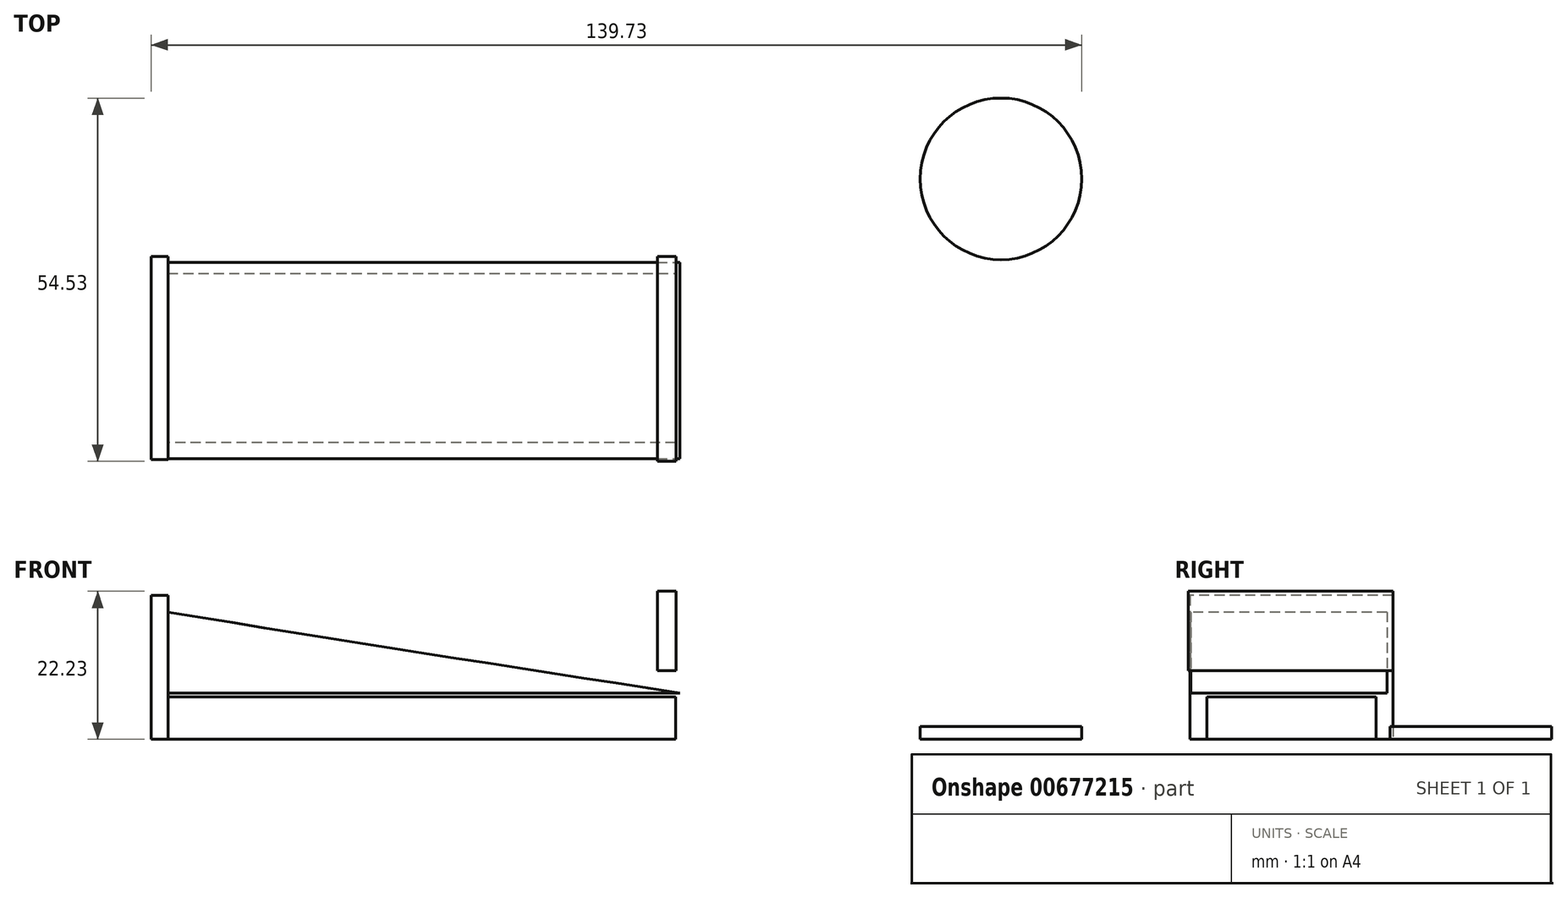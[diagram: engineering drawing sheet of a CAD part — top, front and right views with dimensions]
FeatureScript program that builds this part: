
annotation { "Feature Type Name" : "Feature", "Feature Type Description" : "" }
export const myFeature = defineFeature(function(context is Context, id is Id, definition is map)
    precondition{}
    {
        {
            var Q0;
            Q0=qCreatedBy(makeId("Top.planeOp"),FACE);
            var sketch = newSketch(context, id + "F0", { "sketchPlane" : qUnion([Q0])});
            skLineSegment(sketch, "E0", {"start": v(-99.38, 30.6) * mm, "end": v(-23.18, 30.6) * mm});
            skLineSegment(sketch, "E1", {"start": v(-23.18, 5.2) * mm, "end": v(-99.38, 5.2) * mm});
            skLineSegment(sketch, "E2", {"start": v(-99.38, 30.6) * mm, "end": v(-99.38, 5.2) * mm});
            skLineSegment(sketch, "E3", {"start": v(-23.18, 30.6) * mm, "end": v(-23.18, 5.2) * mm});
            skLineSegment(sketch, "E4.top", {"start": v(-99.38, 33.15) * mm, "end": v(-23.18, 33.15) * mm});
            skLineSegment(sketch, "E4.left", {"start": v(-99.38, 30.6) * mm, "end": v(-99.38, 33.15) * mm});
            skLineSegment(sketch, "E4.right", {"start": v(-23.18, 30.6) * mm, "end": v(-23.18, 33.15) * mm});
            skLineSegment(sketch, "E5.top", {"start": v(-23.18, 2.67) * mm, "end": v(-99.38, 2.67) * mm});
            skLineSegment(sketch, "E5.left", {"start": v(-23.18, 5.2) * mm, "end": v(-23.18, 2.67) * mm});
            skLineSegment(sketch, "E5.right", {"start": v(-99.38, 5.2) * mm, "end": v(-99.38, 2.67) * mm});
            skLineSegment(sketch, "E6.bottom", {"start": v(-99.38, 33.15) * mm, "end": v(-101.92, 33.15) * mm});
            skLineSegment(sketch, "E6.top", {"start": v(-99.38, 2.67) * mm, "end": v(-101.92, 2.67) * mm});
            skLineSegment(sketch, "E6.left", {"start": v(-99.38, 33.15) * mm, "end": v(-99.38, 2.67) * mm});
            skLineSegment(sketch, "E6.right", {"start": v(-101.92, 33.15) * mm, "end": v(-101.92, 2.67) * mm});
            skSolve(sketch);
        }
        {
            var Q0;
            Q0=makeQuery(id+"F0.imprint","IMPRINT",FACE,{"disambiguationData":[TD([[makeQuery(id+"F0.imprint","IMPRINT",EDGE,{"derivedFrom":sQuery(id+"F0.wireOp",EDGE,"E3")}),-1.0]])]});
            extrude(context, id + "F1", {"entities" : qUnion([Q0]), "depth" : 6.35 * mm, "offsetDistance" : 25.4 * mm});
        }
        {
            var Q0;
            {var subQ0=sQuery(id+"F0.wireOp",EDGE,"E0");Q0=makeQuery(id+"F0.imprint","IMPRINT",FACE,{"disambiguationData":[TD([[makeQuery(id+"F0.imprint","IMPRINT",EDGE,{"derivedFrom":subQ0}),1.0]])]});}
            var Q1;
            {var subQ0=sQuery(id+"F0.wireOp",EDGE,"E1");Q1=makeQuery(id+"F0.imprint","IMPRINT",FACE,{"disambiguationData":[TD([[makeQuery(id+"F0.imprint","IMPRINT",EDGE,{"derivedFrom":subQ0}),1.0]])]});}
            var Q2;
            {var subQ3=sQuery(id+"F0.wireOp",EDGE,"E6.bottom");Q2=makeQuery(id+"F0.imprint","IMPRINT",FACE,{"disambiguationData":[TD([[makeQuery(id+"F0.imprint","IMPRINT",EDGE,{"derivedFrom":subQ3}),1.0]])]});}
            extrude(context, id + "F2", {"entities" : qUnion([Q0, Q1, Q2]), "depth" : 19.05 * mm, "offsetDistance" : 25.4 * mm});
        }
        {
            var Q0;
            Q0=qCreatedBy(makeId("Front.planeOp"),FACE);
            var sketch = newSketch(context, id + "F3", { "sketchPlane" : qUnion([Q0])});
            skArc(sketch, "E7", {"start": v(-99.85, 19.18) * mm, "mid": v(-61.2, 12.98) * mm, "end": v(-22.5, 6.97) * mm});
            skLineSegment(sketch, "E8", {"start": v(-99.85, 19.18) * mm, "end": v(-99.85, 6.97) * mm});
            skLineSegment(sketch, "E9", {"start": v(-99.85, 6.97) * mm, "end": v(-22.5, 6.97) * mm});
            skSolve(sketch);
        }
        {
            var Q0;
            Q0=makeQuery(id+"F3.imprint","IMPRINT",FACE,{"disambiguationData":[TD([[makeQuery(id+"F3.imprint","IMPRINT",EDGE,{"derivedFrom":sQuery(id+"F3.wireOp",EDGE,"E7")}),-1.0]])]});
            extrude(context, id + "F4", {"entities" : qUnion([Q0]), "operationType" : NewBodyOperationType.ADD, "oppositeDirection" : true, "depth" : 32.26 * mm, "offsetDistance" : 25.4 * mm});
        }
        {
            var Q0;
            Q0=makeQuery(id+"F4.opExtrude","CAP_FACE",FACE,{"disambiguationData":[OSD([sQuery(id+"F3.wireOp",EDGE,"E7"),sQuery(id+"F3.wireOp",EDGE,"E8"),sQuery(id+"F3.wireOp",EDGE,"E9")])],"isStart":true});
            extrude(context, id + "F5", {"entities" : qUnion([Q0]), "operationType" : NewBodyOperationType.REMOVE, "oppositeDirection" : true, "depth" : 2.8 * mm, "offsetDistance" : 25.4 * mm});
        }
        {
            var Q0;
            {var subQ0=sQuery(id+"F0.wireOp",EDGE,"E1");Q0=makeQuery(id+"F0.imprint","IMPRINT",FACE,{"disambiguationData":[TD([[makeQuery(id+"F0.imprint","IMPRINT",EDGE,{"derivedFrom":subQ0}),1.0]])]});}
            var Q1;
            {var subQ3=sQuery(id+"F0.wireOp",EDGE,"E6.bottom");Q1=makeQuery(id+"F0.imprint","IMPRINT",FACE,{"disambiguationData":[TD([[makeQuery(id+"F0.imprint","IMPRINT",EDGE,{"derivedFrom":subQ3}),1.0]])]});}
            var Q2;
            {var subQ0=sQuery(id+"F0.wireOp",EDGE,"E0");Q2=makeQuery(id+"F0.imprint","IMPRINT",FACE,{"disambiguationData":[TD([[makeQuery(id+"F0.imprint","IMPRINT",EDGE,{"derivedFrom":subQ0}),1.0]])]});}
            extrude(context, id + "F6", {"entities" : qUnion([Q0, Q1, Q2]), "operationType" : NewBodyOperationType.ADD, "depth" : 21.59 * mm, "offsetDistance" : 25.4 * mm});
        }
        {
            var Q0;
            Q0=qCreatedBy(makeId("Right.planeOp"),FACE);
            var sketch = newSketch(context, id + "F7", { "sketchPlane" : qUnion([Q0])});
            skLineSegment(sketch, "E10.bottom", {"start": v(2.41, 22.23) * mm, "end": v(33.15, 22.23) * mm});
            skLineSegment(sketch, "E10.top", {"start": v(2.41, 8.5) * mm, "end": v(33.15, 8.5) * mm});
            skLineSegment(sketch, "E10.left", {"start": v(2.41, 22.23) * mm, "end": v(2.41, 8.5) * mm});
            skLineSegment(sketch, "E10.right", {"start": v(33.15, 22.23) * mm, "end": v(33.15, 8.5) * mm});
            skSolve(sketch);
        }
        {
            var Q0;
            Q0 = qSketchRegion(id + "F7", true);
            extrude(context, id + "F8", {"entities" : qUnion([Q0]), "operationType" : NewBodyOperationType.ADD, "oppositeDirection" : true, "depth" : 25.9 * mm, "offsetDistance" : 25.4 * mm, "hasSecondDirection" : true, "secondDirectionOppositeDirection" : true, "secondDirectionDepth" : 23.1 * mm});
        }
        {
            var Q0;
            Q0=qCreatedBy(makeId("Top.planeOp"),FACE);
            var sketch = newSketch(context, id + "F9", { "sketchPlane" : qUnion([Q0])});
            skCircle(sketch, "E11", {"center": v(25.68, 44.81) * mm, "radius": 12.13 * mm});
            skSolve(sketch);
        }
        {
            var Q0;
            Q0 = qSketchRegion(id + "F9", true);
            extrude(context, id + "F10", {"entities" : qUnion([Q0]), "depth" : 1.9 * mm, "offsetDistance" : 25.4 * mm});
        }
        {
            var Q0;
            Q0=makeQuery(id+"F8.opExtrude","SWEPT_FACE",FACE,{"disambiguationData":[OSD([sQuery(id+"F7.wireOp",EDGE,"E10.top")])]});
            extrude(context, id + "F11", {"entities" : qUnion([Q0]), "operationType" : NewBodyOperationType.REMOVE, "oppositeDirection" : true, "depth" : 1.78 * mm, "offsetDistance" : 25.4 * mm});
        }
    });
